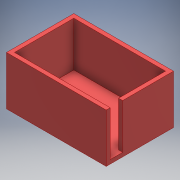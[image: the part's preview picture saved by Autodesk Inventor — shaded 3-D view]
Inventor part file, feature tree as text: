
AUTODESK INVENTOR PART (.ipt)
format: ipt  version: 2018 (Build 220112000, 112)  size: 120,832 bytes
history: native  units: mm
features: extrude x3, sketch x3, projected_geometry x2
ambient origin geometry x8: Origin, YZ Plane, XZ Plane, XY Plane, X Axis, Y Axis, Z Axis, Center Point
bodies: Solid1 (feature_tree)
feature tree (8):
  extrude  "Extrusion1"  Depth=270.0mm
  extrude  "Extrusion2"  Depth=16.0mm
  extrude  "Extrusion3"  Depth=16.0mm
  sketch  "Sketch1"  dims[d0=400.0mm d1=270.0mm]
  sketch  "Sketch2"  dims[d2=16.0mm d3=0.0mm d4=16.0mm]
  projected_geometry  "Projected Loop1"
  sketch  "Sketch3"  dims[d5=16.0mm d6=16.0mm d7=16.0mm d8=180.0mm d9=0.0mm d10=50.0mm d11=180.0mm d12=0.0mm]
  projected_geometry  "Projected Loop2"
